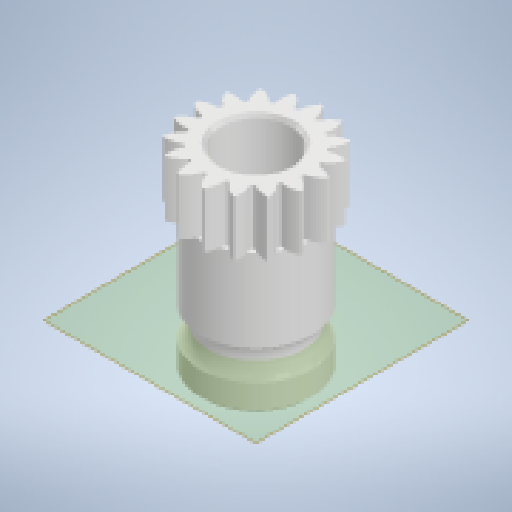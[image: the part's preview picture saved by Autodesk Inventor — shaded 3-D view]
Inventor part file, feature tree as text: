
AUTODESK INVENTOR PART (.ipt)
format: ipt  version: 2024 (Build 280153000, 153)  size: 290,304 bytes
history: native  units: mm
features: plane x1
ambient origin geometry x8: Origin, YZ Plane, XZ Plane, XY Plane, X Axis, Y Axis, Z Axis, Center Point
bodies: Solid1 (feature_tree), Body1 (feature_tree)
feature tree (1):
  plane  "Work Plane1"
